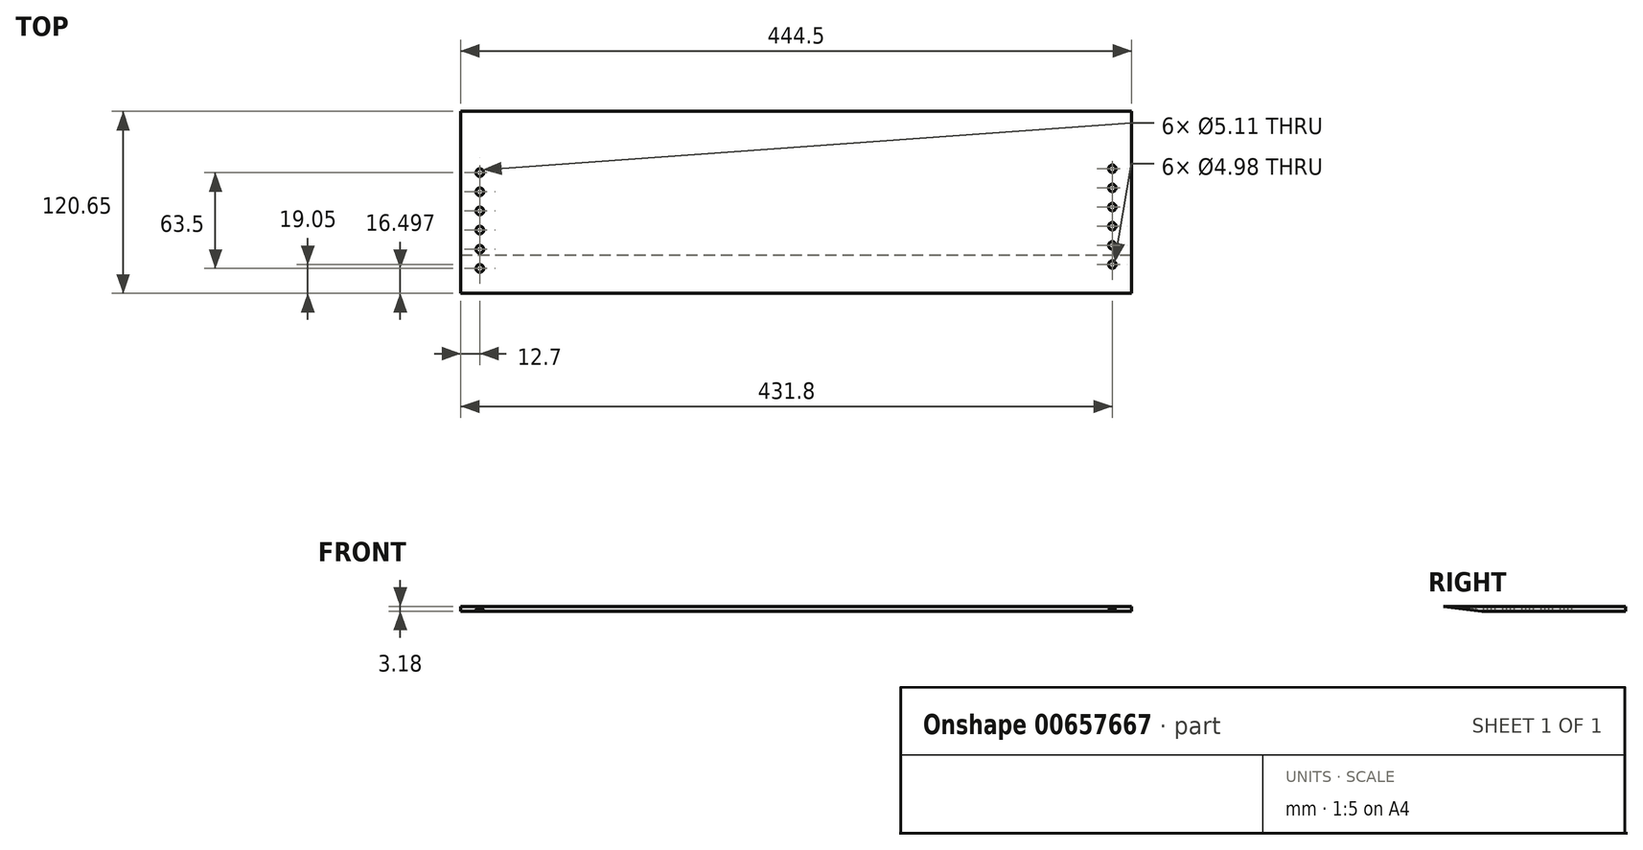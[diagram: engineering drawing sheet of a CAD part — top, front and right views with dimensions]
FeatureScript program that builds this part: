
annotation { "Feature Type Name" : "Feature", "Feature Type Description" : "" }
export const myFeature = defineFeature(function(context is Context, id is Id, definition is map)
    precondition{}
    {
        {
            var Q0;
            Q0=qCreatedBy(makeId("Top.planeOp"),FACE);
            var sketch = newSketch(context, id + "F0", { "sketchPlane" : qUnion([Q0])});
            skLineSegment(sketch, "E0.bottom", {"start": v(0, 0) * mm, "end": v(444.5, 0) * mm});
            skLineSegment(sketch, "E0.top", {"start": v(0, -127) * mm, "end": v(444.5, -127) * mm});
            skLineSegment(sketch, "E0.left", {"start": v(0, 0) * mm, "end": v(0, -127) * mm});
            skLineSegment(sketch, "E0.right", {"start": v(444.5, 0) * mm, "end": v(444.5, -127) * mm});
            skSolve(sketch);
        }
        {
            var Q0;
            Q0=makeQuery(id+"F0.imprint","IMPRINT",FACE,{"disambiguationData":[TD([[makeQuery(id+"F0.imprint","IMPRINT",EDGE,{"derivedFrom":sQuery(id+"F0.wireOp",EDGE,"E0.bottom")}),-1.0]])]});
            extrude(context, id + "F1", {"entities" : qUnion([Q0]), "depth" : 3.17 * mm, "offsetDistance" : 25.4 * mm});
        }
        {
            var Q0;
            Q0=makeQuery(id+"F1.opExtrude","CAP_FACE",FACE,{"disambiguationData":[OSD([sQuery(id+"F0.wireOp",EDGE,"E0.bottom"),sQuery(id+"F0.wireOp",EDGE,"E0.top"),sQuery(id+"F0.wireOp",EDGE,"E0.left"),sQuery(id+"F0.wireOp",EDGE,"E0.right")])],"isStart":false});
            var sketch = newSketch(context, id + "F2", { "sketchPlane" : qUnion([Q0])});
            skCircle(sketch, "E1", {"center": v(431.8, -101.6) * mm, "radius": 2.49 * mm});
            skCircle(sketch, "E2.0.1.0", {"center": v(431.8, -88.9) * mm, "radius": 2.49 * mm});
            skCircle(sketch, "E2.0.2.0", {"center": v(431.8, -76.2) * mm, "radius": 2.49 * mm});
            skCircle(sketch, "E2.0.3.0", {"center": v(431.8, -63.5) * mm, "radius": 2.49 * mm});
            skCircle(sketch, "E2.0.4.0", {"center": v(431.8, -50.8) * mm, "radius": 2.49 * mm});
            skLineSegment(sketch, "E2.direction1", {"start": v(352.43, -101.6) * mm, "end": v(431.8, -101.6) * mm, "construction": true});
            skLineSegment(sketch, "E2.direction2", {"start": v(431.8, -101.6) * mm, "end": v(431.8, -88.9) * mm, "construction": true});
            skCircle(sketch, "E3", {"center": v(12.7, -104.15) * mm, "radius": 2.55 * mm});
            skCircle(sketch, "E4.0.1.0", {"center": v(12.7, -91.45) * mm, "radius": 2.55 * mm});
            skCircle(sketch, "E4.0.2.0", {"center": v(12.7, -78.75) * mm, "radius": 2.55 * mm});
            skCircle(sketch, "E4.0.3.0", {"center": v(12.7, -66.05) * mm, "radius": 2.55 * mm});
            skCircle(sketch, "E4.0.4.0", {"center": v(12.7, -53.35) * mm, "radius": 2.55 * mm});
            skLineSegment(sketch, "E4.direction1", {"start": v(12.7, -104.15) * mm, "end": v(53.98, -104.15) * mm, "construction": true});
            skLineSegment(sketch, "E4.direction2", {"start": v(12.7, -104.15) * mm, "end": v(12.7, -91.45) * mm, "construction": true});
            skCircle(sketch, "E5.0.0.5", {"center": v(12.7, -40.65) * mm, "radius": 2.55 * mm});
            skCircle(sketch, "E6.0.0.5", {"center": v(431.8, -38.1) * mm, "radius": 2.49 * mm});
            skSolve(sketch);
        }
        {
            var Q0;
            Q0=makeQuery(id+"F2.imprint","IMPRINT",FACE,{"disambiguationData":[TD([[makeQuery(id+"F2.imprint","IMPRINT",EDGE,{"derivedFrom":sQuery(id+"F2.wireOp",EDGE,"E3")}),1.0]])]});
            var Q1;
            Q1=makeQuery(id+"F2.imprint","IMPRINT",FACE,{"disambiguationData":[TD([[makeQuery(id+"F2.imprint","IMPRINT",EDGE,{"derivedFrom":sQuery(id+"F2.wireOp",EDGE,"E4.0.1.0")}),1.0]])]});
            var Q2;
            Q2=makeQuery(id+"F2.imprint","IMPRINT",FACE,{"disambiguationData":[TD([[makeQuery(id+"F2.imprint","IMPRINT",EDGE,{"derivedFrom":sQuery(id+"F2.wireOp",EDGE,"E4.0.2.0")}),1.0]])]});
            var Q3;
            Q3=makeQuery(id+"F2.imprint","IMPRINT",FACE,{"disambiguationData":[TD([[makeQuery(id+"F2.imprint","IMPRINT",EDGE,{"derivedFrom":sQuery(id+"F2.wireOp",EDGE,"E4.0.3.0")}),1.0]])]});
            var Q4;
            Q4=makeQuery(id+"F2.imprint","IMPRINT",FACE,{"disambiguationData":[TD([[makeQuery(id+"F2.imprint","IMPRINT",EDGE,{"derivedFrom":sQuery(id+"F2.wireOp",EDGE,"E4.0.4.0")}),1.0]])]});
            var Q5;
            Q5=makeQuery(id+"F2.imprint","IMPRINT",FACE,{"disambiguationData":[TD([[makeQuery(id+"F2.imprint","IMPRINT",EDGE,{"derivedFrom":sQuery(id+"F2.wireOp",EDGE,"E1")}),1.0]])]});
            var Q6;
            Q6=makeQuery(id+"F2.imprint","IMPRINT",FACE,{"disambiguationData":[TD([[makeQuery(id+"F2.imprint","IMPRINT",EDGE,{"derivedFrom":sQuery(id+"F2.wireOp",EDGE,"E2.0.1.0")}),1.0]])]});
            var Q7;
            Q7=makeQuery(id+"F2.imprint","IMPRINT",FACE,{"disambiguationData":[TD([[makeQuery(id+"F2.imprint","IMPRINT",EDGE,{"derivedFrom":sQuery(id+"F2.wireOp",EDGE,"E2.0.2.0")}),1.0]])]});
            var Q8;
            Q8=makeQuery(id+"F2.imprint","IMPRINT",FACE,{"disambiguationData":[TD([[makeQuery(id+"F2.imprint","IMPRINT",EDGE,{"derivedFrom":sQuery(id+"F2.wireOp",EDGE,"E2.0.3.0")}),1.0]])]});
            var Q9;
            Q9=makeQuery(id+"F2.imprint","IMPRINT",FACE,{"disambiguationData":[TD([[makeQuery(id+"F2.imprint","IMPRINT",EDGE,{"derivedFrom":sQuery(id+"F2.wireOp",EDGE,"E2.0.4.0")}),1.0]])]});
            var Q10;
            Q10=makeQuery(id+"F2.imprint","IMPRINT",FACE,{"disambiguationData":[TD([[makeQuery(id+"F2.imprint","IMPRINT",EDGE,{"derivedFrom":sQuery(id+"F2.wireOp",EDGE,"E5.0.0.5")}),1.0]])]});
            var Q11;
            Q11=makeQuery(id+"F2.imprint","IMPRINT",FACE,{"disambiguationData":[TD([[makeQuery(id+"F2.imprint","IMPRINT",EDGE,{"derivedFrom":sQuery(id+"F2.wireOp",EDGE,"E6.0.0.5")}),1.0]])]});
            extrude(context, id + "F3", {"entities" : qUnion([Q0, Q1, Q2, Q3, Q4, Q5, Q6, Q7, Q8, Q9, Q10, Q11]), "operationType" : NewBodyOperationType.REMOVE, "oppositeDirection" : true, "depth" : 25.4 * mm, "offsetDistance" : 25.4 * mm});
        }
        {
            var Q0;
            Q0=makeQuery(id+"F1.opExtrude","SWEPT_FACE",FACE,{"disambiguationData":[OSD([sQuery(id+"F0.wireOp",EDGE,"E0.right")])]});
            var sketch = newSketch(context, id + "F4", { "sketchPlane" : qUnion([Q0])});
            skLineSegment(sketch, "E7", {"start": v(-120.65, 3.17) * mm, "end": v(-95.25, 0) * mm});
            skSolve(sketch);
        }
        {
            var Q0;
            {var subQ0=sQuery(id+"F4.wireOp",EDGE,"rp3jMHPP-lLZH-RVnD-oOak-bK0siXgC1Ux6");Q0=makeQuery(id+"F4.imprint","IMPRINT",FACE,{"disambiguationData":[TD([[makeQuery(id+"F4.imprint","IMPRINT",EDGE,{"derivedFrom":subQ0}),1.0]])]});}
            var Q1;
            {var subQ0=sQuery(id+"F4.wireOp",EDGE,"E7");Q1=makeQuery(id+"F4.imprint","IMPRINT",FACE,{"disambiguationData":[TD([[makeQuery(id+"F4.imprint","IMPRINT",EDGE,{"derivedFrom":subQ0}),-1.0]])]});}
            extrude(context, id + "F5", {"entities" : qUnion([Q0, Q1]), "operationType" : NewBodyOperationType.REMOVE, "endBound" : BoundingType.THROUGH_ALL, "oppositeDirection" : true, "depth" : 25.4 * mm, "offsetDistance" : 25.4 * mm});
        }
    });
